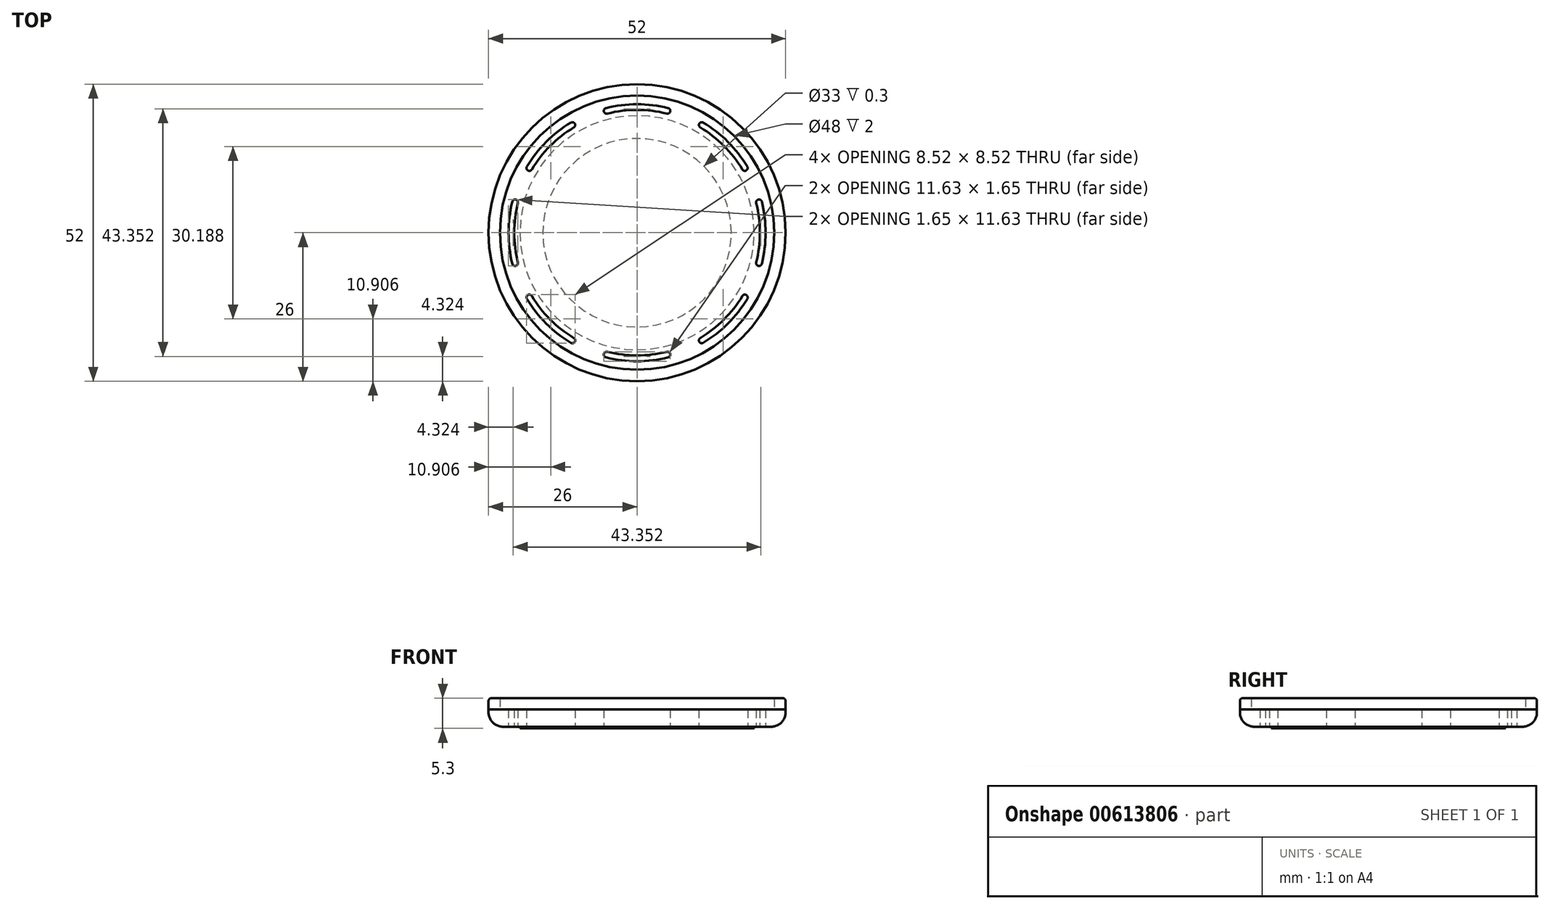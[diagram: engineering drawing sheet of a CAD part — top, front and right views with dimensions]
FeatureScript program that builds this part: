
annotation { "Feature Type Name" : "Feature", "Feature Type Description" : "" }
export const myFeature = defineFeature(function(context is Context, id is Id, definition is map)
    precondition{}
    {
        {
            var Q0;
            Q0=qCreatedBy(makeId("Top.planeOp"),FACE);
            var sketch = newSketch(context, id + "F0", { "sketchPlane" : qUnion([Q0])});
            skCircle(sketch, "E0", {"center": v(0, 0) * mm, "radius": 26 * mm});
            skCircle(sketch, "E1", {"center": v(0, 0) * mm, "radius": 22.5 * mm});
            skCircle(sketch, "E2", {"center": v(0, 0) * mm, "radius": 22 * mm, "construction": true});
            skLineSegment(sketch, "E3", {"start": v(0, 0) * mm, "end": v(35.44, 8.84) * mm, "construction": true});
            skLineSegment(sketch, "E4", {"start": v(0, 0) * mm, "end": v(35.8, 0) * mm, "construction": true});
            skLineSegment(sketch, "E5", {"start": v(0, 0) * mm, "end": v(35.9, -8.95) * mm, "construction": true});
            skCircle(sketch, "E6", {"center": v(21.35, 5.32) * mm, "radius": 0.5 * mm});
            skCircle(sketch, "E7", {"center": v(21.35, -5.32) * mm, "radius": 0.5 * mm});
            skCircle(sketch, "E8", {"center": v(0, 0) * mm, "radius": 21.5 * mm});
            skCircle(sketch, "E9", {"center": v(0, 0) * mm, "radius": 20.5 * mm});
            skCircle(sketch, "E10", {"center": v(0, 0) * mm, "radius": 16.5 * mm});
            skLineSegment(sketch, "E11", {"start": v(0, 0) * mm, "end": v(8.94, -35.84) * mm, "construction": true});
            skLineSegment(sketch, "E12", {"start": v(0, 0) * mm, "end": v(-9.17, -36.8) * mm, "construction": true});
            skLineSegment(sketch, "E13", {"start": v(0, 0) * mm, "end": v(0, -38.75) * mm, "construction": true});
            skLineSegment(sketch, "E14", {"start": v(0, 0) * mm, "end": v(0, 31.62) * mm, "construction": true});
            skLineSegment(sketch, "E15", {"start": v(0, 0) * mm, "end": v(-37.84, 0) * mm, "construction": true});
            skLineSegment(sketch, "E16", {"start": v(0, 0) * mm, "end": v(-36.14, -9) * mm, "construction": true});
            skLineSegment(sketch, "E17", {"start": v(0, 0) * mm, "end": v(-35.94, 8.96) * mm, "construction": true});
            skLineSegment(sketch, "E18", {"start": v(0, 0) * mm, "end": v(7.97, 31.97) * mm, "construction": true});
            skLineSegment(sketch, "E19", {"start": v(0, 0) * mm, "end": v(-7.78, 31.22) * mm, "construction": true});
            skCircle(sketch, "E20", {"center": v(5.32, 21.35) * mm, "radius": 0.5 * mm});
            skCircle(sketch, "E21", {"center": v(-5.32, 21.35) * mm, "radius": 0.5 * mm});
            skCircle(sketch, "E22", {"center": v(-21.35, 5.32) * mm, "radius": 0.5 * mm});
            skCircle(sketch, "E23", {"center": v(-21.35, -5.32) * mm, "radius": 0.5 * mm});
            skCircle(sketch, "E24", {"center": v(5.32, -21.35) * mm, "radius": 0.5 * mm});
            skCircle(sketch, "E25", {"center": v(-5.32, -21.35) * mm, "radius": 0.5 * mm});
            skLineSegment(sketch, "E26", {"start": v(0, 0) * mm, "end": v(30.1, -30.1) * mm, "construction": true});
            skLineSegment(sketch, "E27", {"start": v(0, 0) * mm, "end": v(29.3, -17.6) * mm, "construction": true});
            skLineSegment(sketch, "E28", {"start": v(0, 0) * mm, "end": v(16.92, -28.15) * mm, "construction": true});
            skCircle(sketch, "E29", {"center": v(18.86, -11.33) * mm, "radius": 0.5 * mm});
            skCircle(sketch, "E30", {"center": v(11.33, -18.86) * mm, "radius": 0.5 * mm});
            skLineSegment(sketch, "E31", {"start": v(0, 0) * mm, "end": v(28.4, 28.4) * mm, "construction": true});
            skLineSegment(sketch, "E32", {"start": v(0, 0) * mm, "end": v(32.29, 19.4) * mm, "construction": true});
            skLineSegment(sketch, "E33", {"start": v(0, 0) * mm, "end": v(17.58, 29.26) * mm, "construction": true});
            skCircle(sketch, "E34", {"center": v(18.86, 11.33) * mm, "radius": 0.5 * mm});
            skCircle(sketch, "E35", {"center": v(11.33, 18.86) * mm, "radius": 0.5 * mm});
            skLineSegment(sketch, "E36", {"start": v(0, 0) * mm, "end": v(-27.32, 27.32) * mm, "construction": true});
            skLineSegment(sketch, "E37", {"start": v(0, 0) * mm, "end": v(-18.14, 30.18) * mm, "construction": true});
            skLineSegment(sketch, "E38", {"start": v(0, 0) * mm, "end": v(-29.38, 17.65) * mm, "construction": true});
            skLineSegment(sketch, "E39", {"start": v(0, 0) * mm, "end": v(-27.25, -27.25) * mm, "construction": true});
            skCircle(sketch, "E40", {"center": v(-11.33, 18.86) * mm, "radius": 0.5 * mm});
            skCircle(sketch, "E41", {"center": v(-18.86, 11.33) * mm, "radius": 0.5 * mm});
            skLineSegment(sketch, "E42", {"start": v(0, 0) * mm, "end": v(-32.11, -19.3) * mm, "construction": true});
            skLineSegment(sketch, "E43", {"start": v(0, 0) * mm, "end": v(-18.3, -30.47) * mm, "construction": true});
            skCircle(sketch, "E44", {"center": v(-18.86, -11.33) * mm, "radius": 0.5 * mm});
            skCircle(sketch, "E45", {"center": v(-11.33, -18.86) * mm, "radius": 0.5 * mm});
            skCircle(sketch, "E46", {"center": v(0, 0) * mm, "radius": 24 * mm});
            skSolve(sketch);
        }
        {
            var Q0;
            Q0=makeQuery(id+"F0.imprint","IMPRINT",FACE,{"disambiguationData":[TD([[makeQuery(id+"F0.imprint","IMPRINT",EDGE,{"derivedFrom":sQuery(id+"F0.wireOp",EDGE,"E0")}),1.0]])]});
            extrude(context, id + "F1", {"entities" : qUnion([Q0]), "depth" : 5 * mm, "offsetDistance" : 25 * mm, "hasSecondDirection" : true, "secondDirectionOppositeDirection" : true, "secondDirectionDepth" : -3 * mm});
        }
        {
            var Q0;
            Q0 = qSketchRegion(id + "F0", true);
            var Q1;
            Q1=makeQuery(id+"F0.imprint","IMPRINT",FACE,{"disambiguationData":[TD([[makeQuery(id+"F0.imprint","IMPRINT",EDGE,{"derivedFrom":sQuery(id+"F0.wireOp",EDGE,"E10")}),1.0]])]});
            var Q2;
            Q2=makeQuery(id+"F0.imprint","IMPRINT",FACE,{"disambiguationData":[TD([[makeQuery(id+"F0.imprint","IMPRINT",EDGE,{"derivedFrom":sQuery(id+"F0.wireOp",EDGE,"E9")}),1.0]])]});
            var Q3;
            Q3=makeQuery(id+"F0.imprint","IMPRINT",FACE,{"disambiguationData":[TD([[makeQuery(id+"F0.imprint","IMPRINT",EDGE,{"derivedFrom":sQuery(id+"F0.wireOp",EDGE,"E9")}),-1.0]])]});
            var Q4;
            {var subQ0=sQuery(id+"F0.wireOp",EDGE,"E41");var subQ1=sQuery(id+"F0.wireOp",EDGE,"E1");var subQ2=makeQuery(id+"F0.imprint","INTERSECT",VERTEX,{"derivedFrom":[subQ1,subQ0]});Q4=makeQuery(id+"F0.imprint","IMPRINT",FACE,{"disambiguationData":[TD([[makeQuery(id+"F0.imprint","IMPRINT",EDGE,{"disambiguationData":[TD([[subQ2,-1.0]])],"derivedFrom":subQ1}),1.0]])]});}
            var Q5;
            Q5=makeQuery(id+"F0.imprint","IMPRINT",FACE,{"disambiguationData":[TD([[makeQuery(id+"F0.imprint","IMPRINT",EDGE,{"derivedFrom":sQuery(id+"F0.wireOp",EDGE,"E46")}),1.0]])]});
            var Q6;
            {var subQ0=sQuery(id+"F0.wireOp",EDGE,"E21");var subQ1=sQuery(id+"F0.wireOp",EDGE,"E1");var subQ2=makeQuery(id+"F0.imprint","INTERSECT",VERTEX,{"derivedFrom":[subQ1,subQ0]});Q6=makeQuery(id+"F0.imprint","IMPRINT",FACE,{"disambiguationData":[TD([[makeQuery(id+"F0.imprint","IMPRINT",EDGE,{"disambiguationData":[TD([[subQ2,-1.0]])],"derivedFrom":subQ1}),1.0]])]});}
            var Q7;
            {var subQ0=sQuery(id+"F0.wireOp",EDGE,"E35");var subQ1=sQuery(id+"F0.wireOp",EDGE,"E1");var subQ2=makeQuery(id+"F0.imprint","INTERSECT",VERTEX,{"derivedFrom":[subQ1,subQ0]});Q7=makeQuery(id+"F0.imprint","IMPRINT",FACE,{"disambiguationData":[TD([[makeQuery(id+"F0.imprint","IMPRINT",EDGE,{"disambiguationData":[TD([[subQ2,-1.0]])],"derivedFrom":subQ1}),1.0]])]});}
            var Q8;
            {var subQ0=sQuery(id+"F0.wireOp",EDGE,"E34");var subQ1=sQuery(id+"F0.wireOp",EDGE,"E1");var subQ2=makeQuery(id+"F0.imprint","INTERSECT",VERTEX,{"derivedFrom":[subQ1,subQ0]});Q8=makeQuery(id+"F0.imprint","IMPRINT",FACE,{"disambiguationData":[TD([[makeQuery(id+"F0.imprint","IMPRINT",EDGE,{"disambiguationData":[TD([[subQ2,1.0]])],"derivedFrom":subQ1}),1.0]])]});}
            var Q9;
            {var subQ0=sQuery(id+"F0.wireOp",EDGE,"E29");var subQ1=sQuery(id+"F0.wireOp",EDGE,"E1");var subQ2=makeQuery(id+"F0.imprint","INTERSECT",VERTEX,{"derivedFrom":[subQ1,subQ0]});Q9=makeQuery(id+"F0.imprint","IMPRINT",FACE,{"disambiguationData":[TD([[makeQuery(id+"F0.imprint","IMPRINT",EDGE,{"disambiguationData":[TD([[subQ2,-1.0]])],"derivedFrom":subQ1}),1.0]])]});}
            var Q10;
            {var subQ0=sQuery(id+"F0.wireOp",EDGE,"E24");var subQ1=sQuery(id+"F0.wireOp",EDGE,"E1");var subQ2=makeQuery(id+"F0.imprint","INTERSECT",VERTEX,{"derivedFrom":[subQ1,subQ0]});Q10=makeQuery(id+"F0.imprint","IMPRINT",FACE,{"disambiguationData":[TD([[makeQuery(id+"F0.imprint","IMPRINT",EDGE,{"disambiguationData":[TD([[subQ2,-1.0]])],"derivedFrom":subQ1}),1.0]])]});}
            var Q11;
            {var subQ0=sQuery(id+"F0.wireOp",EDGE,"E45");var subQ1=sQuery(id+"F0.wireOp",EDGE,"E1");var subQ2=makeQuery(id+"F0.imprint","INTERSECT",VERTEX,{"derivedFrom":[subQ1,subQ0]});Q11=makeQuery(id+"F0.imprint","IMPRINT",FACE,{"disambiguationData":[TD([[makeQuery(id+"F0.imprint","IMPRINT",EDGE,{"disambiguationData":[TD([[subQ2,-1.0]])],"derivedFrom":subQ1}),1.0]])]});}
            var Q12;
            {var subQ0=sQuery(id+"F0.wireOp",EDGE,"E23");var subQ1=sQuery(id+"F0.wireOp",EDGE,"E1");var subQ2=makeQuery(id+"F0.imprint","INTERSECT",VERTEX,{"derivedFrom":[subQ1,subQ0]});Q12=makeQuery(id+"F0.imprint","IMPRINT",FACE,{"disambiguationData":[TD([[makeQuery(id+"F0.imprint","IMPRINT",EDGE,{"disambiguationData":[TD([[subQ2,-1.0]])],"derivedFrom":subQ1}),1.0]])]});}
            extrude(context, id + "F2", {"entities" : qUnion([Q0, Q1, Q2, Q3, Q4, Q5, Q6, Q7, Q8, Q9, Q10, Q11, Q12]), "depth" : 3 * mm, "offsetDistance" : 25 * mm});
        }
        {
            var Q0;
            Q0=makeQuery(id+"F2.opExtrude","CAP_EDGE",EDGE,{"disambiguationData":[OSD([sQuery(id+"F0.wireOp",EDGE,"E0")])],"isStart":true});
            fillet(context, id + "F3", {"entities" : qUnion([Q0]), "radius" : 2.5 * mm, "tangentPropagation" : true, "allowEdgeOverflow" : false});
        }
        {
            var Q0;
            Q0=makeQuery(id+"F1.opExtrude","CAP_EDGE",EDGE,{"disambiguationData":[OSD([sQuery(id+"F0.wireOp",EDGE,"E0")])],"isStart":false});
            fillet(context, id + "F4", {"entities" : qUnion([Q0]), "radius" : 0.5 * mm, "tangentPropagation" : true, "allowEdgeOverflow" : false});
        }
        {
            var Q0;
            Q0=makeQuery(id+"F0.imprint","IMPRINT",FACE,{"disambiguationData":[TD([[makeQuery(id+"F0.imprint","IMPRINT",EDGE,{"derivedFrom":sQuery(id+"F0.wireOp",EDGE,"E9")}),1.0]])]});
            extrude(context, id + "F5", {"entities" : qUnion([Q0]), "depth" : -0.3 * mm, "offsetDistance" : 25 * mm});
        }
    });
